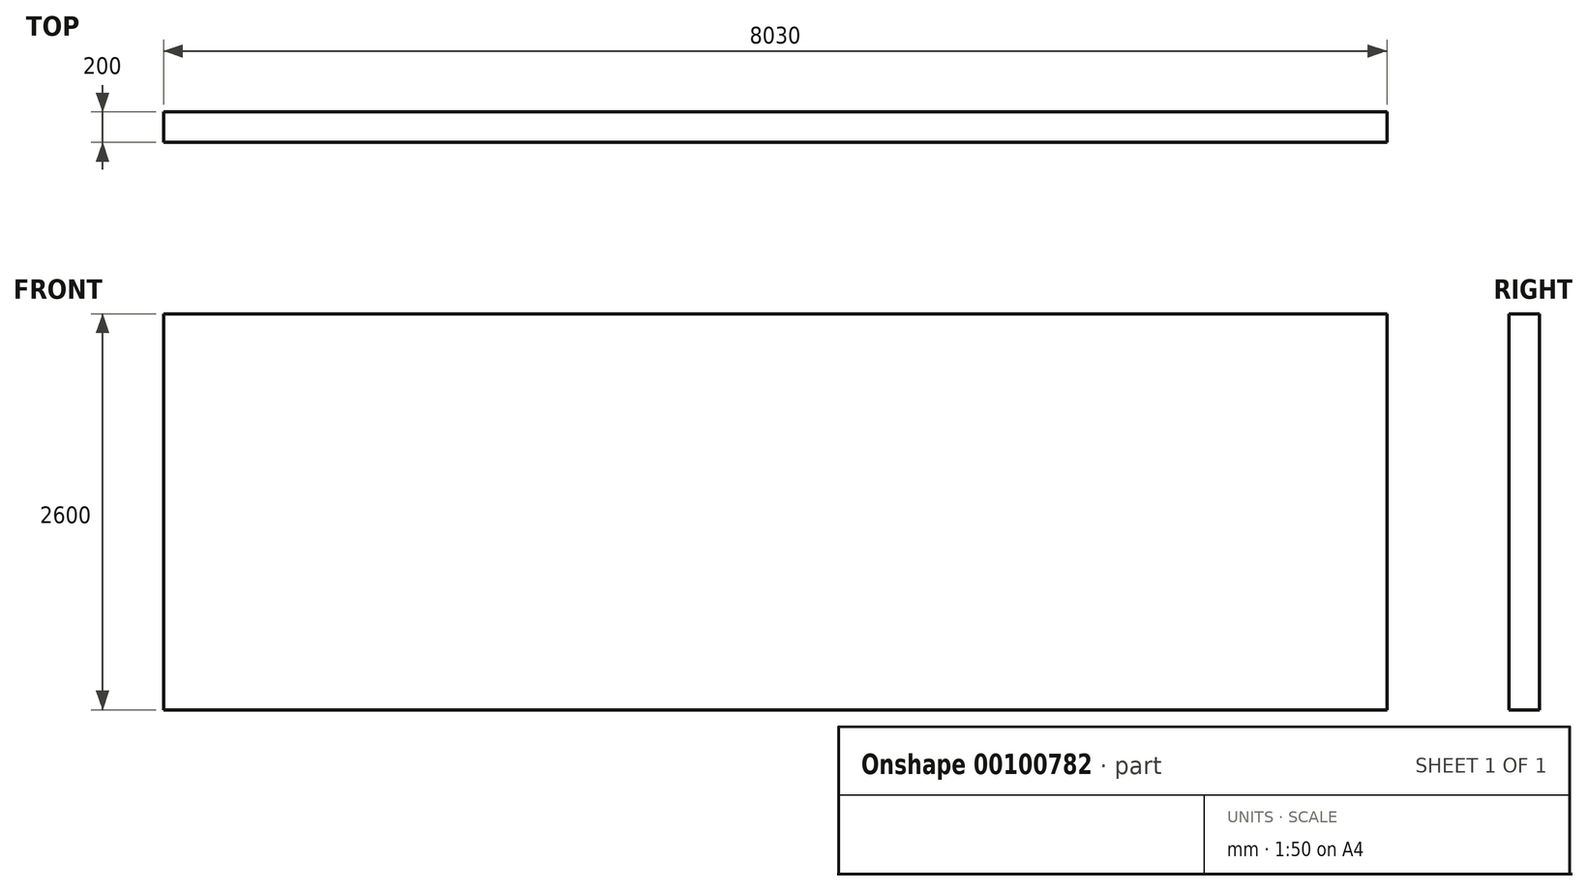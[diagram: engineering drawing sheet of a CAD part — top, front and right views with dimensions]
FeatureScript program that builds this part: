
annotation { "Feature Type Name" : "Feature", "Feature Type Description" : "" }
export const myFeature = defineFeature(function(context is Context, id is Id, definition is map)
    precondition{}
    {
        {
            var Q0;
            Q0=qCreatedBy(makeId("Front.planeOp"),FACE);
            var sketch = newSketch(context, id + "F0", { "sketchPlane" : qUnion([Q0])});
            skLineSegment(sketch, "E0.bottom", {"start": v(-4012.84, 575.51) * mm, "end": v(4017.16, 575.51) * mm});
            skLineSegment(sketch, "E0.top", {"start": v(-4012.84, -2024.49) * mm, "end": v(4017.16, -2024.49) * mm});
            skLineSegment(sketch, "E0.left", {"start": v(-4012.84, 575.51) * mm, "end": v(-4012.84, -2024.49) * mm});
            skLineSegment(sketch, "E0.right", {"start": v(4017.16, 575.51) * mm, "end": v(4017.16, -2024.49) * mm});
            skSolve(sketch);
        }
        {
            var Q0;
            Q0 = qSketchRegion(id + "F0", true);
            extrude(context, id + "F1", {"entities" : qUnion([Q0]), "depth" : 200 * mm});
        }
    });
